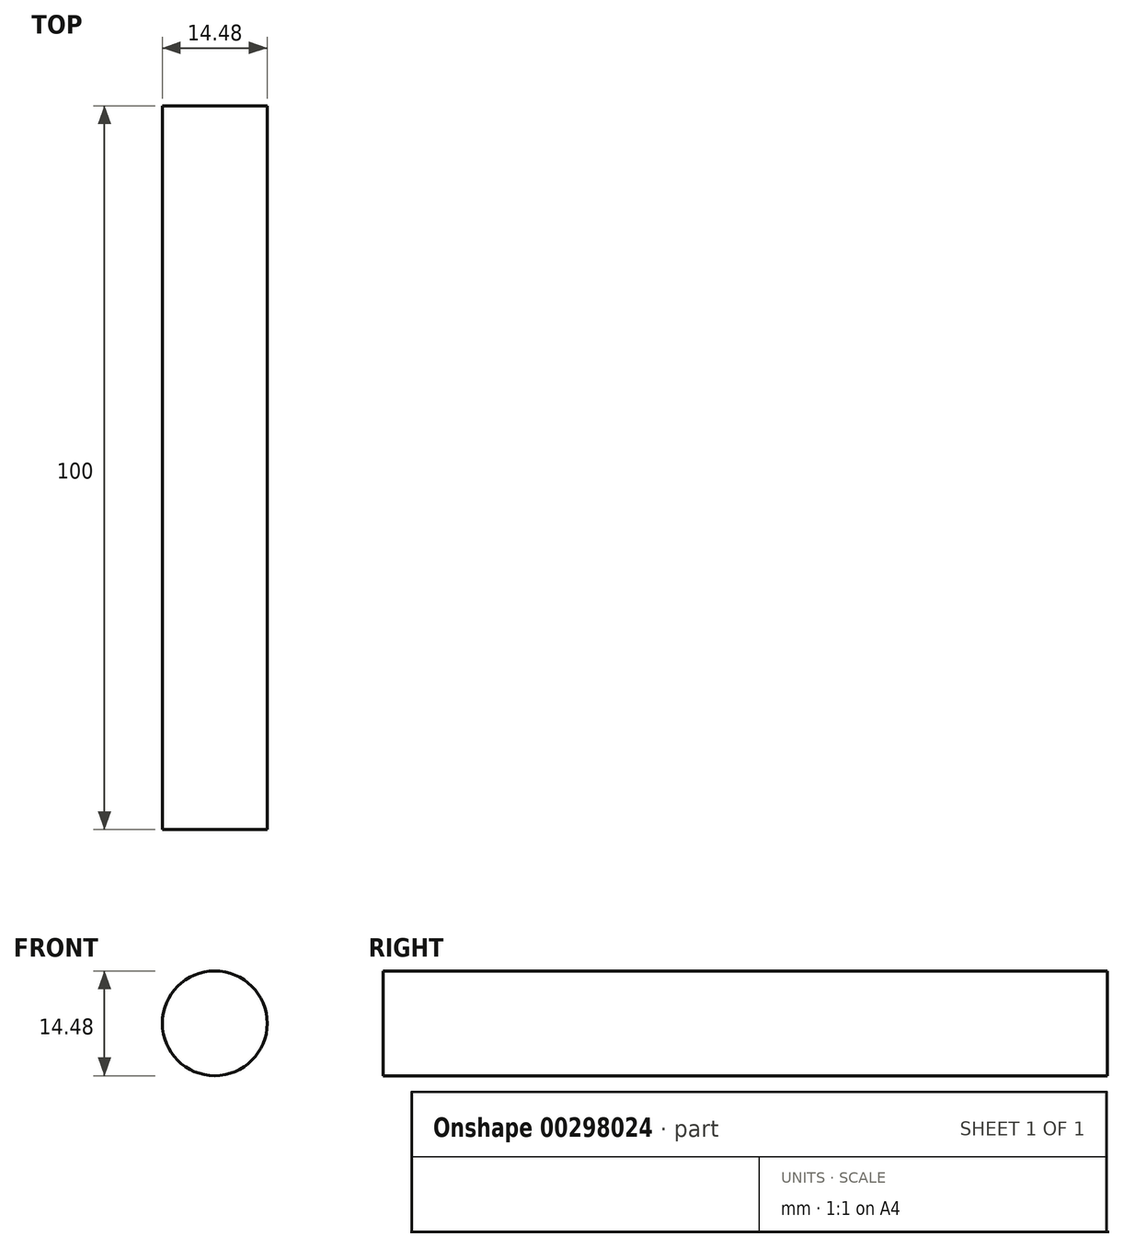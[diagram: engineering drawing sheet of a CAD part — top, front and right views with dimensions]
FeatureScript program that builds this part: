
annotation { "Feature Type Name" : "Feature", "Feature Type Description" : "" }
export const myFeature = defineFeature(function(context is Context, id is Id, definition is map)
    precondition{}
    {
        {
            var Q0;
            Q0=qCreatedBy(makeId("Front.planeOp"),FACE);
            var sketch = newSketch(context, id + "F0", { "sketchPlane" : qUnion([Q0])});
            skCircle(sketch, "E0", {"center": v(0, 0) * mm, "radius": 7.24 * mm});
            skSolve(sketch);
        }
        {
            var Q0;
            Q0=makeQuery(id+"F0.imprint","IMPRINT",FACE,{"disambiguationData":[TD([[makeQuery(id+"F0.imprint","IMPRINT",EDGE,{"derivedFrom":sQuery(id+"F0.wireOp",EDGE,"E0")}),1.0]])]});
            extrude(context, id + "F1", {"entities" : qUnion([Q0]), "depth" : 100 * mm});
        }
        {
            var Q0;
            Q0 = qSketchRegion(id + "F0", true);
            extrude(context, id + "F2", {"entities" : qUnion([Q0]), "operationType" : NewBodyOperationType.ADD, "depth" : 25.4 * mm});
        }
    });
